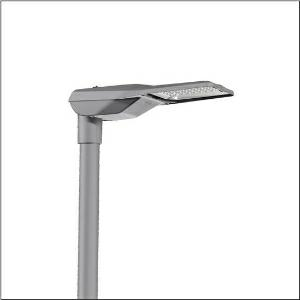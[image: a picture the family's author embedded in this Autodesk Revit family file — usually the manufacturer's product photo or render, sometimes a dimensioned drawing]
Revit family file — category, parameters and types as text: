
# Revit family: streetlight_sl_21_mini___p0_8a_5xe2u33s08gb_2c4a
name_source: partatom
category: Lighting Fixtures
units: mm (PartAtom-declared; Revit-internal decimal feet)

## family parameters
Cut with Voids When Loaded = No
Host = Face
Light Source = No
Part Type = Normal
Room Calculation Point = No
Round Connector Dimension = Use Diameter
Shared = No

## types (1)
- --- (1 x LED, 5990 lm, 40.4 W, 3000K)
    Apparent Load = 40 VA
    CIE Flux Codes = 33 69 96 100 100
    Color Rendering = 70
    Color Temperature = 3000K
    Default Elevation = 1800 mm
    Description = Streetlight SL 21 mini, mast luminaire, primary light control with lens, of PMMA, primary optical cover: cover, of toughened safety glass, transparent, light distribution: P0.8a, light emission: direct distribution, primary light characteristic: asymmetric, installation type: post-top, side-entry, LED, High Power LED, rated luminous flux: 5.990lm, luminous efficacy: 148lm/W, light colour: 730, colour temperature: 3000K, control gear: D4i, control: pre-setting: logarithmic dimming characteristic, flexible luminous flux parameterisation, time-dependent luminous flux control, constant luminous flux control, overheat protection, mains connection: 220..240V, AC, 50/60Hz, start of lifetime: 40W, end of service life: 41W, reduction: 19W, luminaire housing, of diecast aluminium, powder-coated, SITECO metallic grey (DB 702S), corrosivity category C5 high according to DIN EN ISO 12944, multi-level sealing system, sealing non-destructively replaceable, inclination adjustable: 0°, 5°, 10°, 15°, please order mast flange separately, length: 628mm, width: 235mm, height: 110mm, mast flange for spigot size: 42mm (side-entry): 5XC10008XM4, 60/48mm (side-entry/post-top): 5XC10108XM2, 76/60mm (side-entry/post-top): 5XC10108XM1, mounting height: 4..8m, Smart Interface above, protection rating (complete): IP66, insulation class (complete): insulation class II (safety insulation), certification: CE, ENEC, ENEC+, VDE, impact resistance: IK10, permissible operating ambient temperature for outdoor applications: -40..+50°C, standard-compliant lighting for roads and squares, packaging unit: 1 piece

Light Distribution: P0.8a
    Height = 110 mm
    Lamp = 1 x LED
    Lamp Light Flux = 5990 lm
    Lamp Power = 40.4 W
    Lamp count = 1
    Length = 625 mm
    Luminous efficacy = 148 lm/W
    Manufacturer = Siteco
    ModVariant = No
    Model = 5XE2U33S08GB
    Number of Poles = 1
    OnlyDefault = Yes
    Power Factor = 1
    Product Name = Streetlight SL 21 mini | P0.8a
    Product group = mast luminaire | pylon top
    ProductGroupID = 6100
    Protection Class = Protection class II
    Protection Degree = IP 66
    RLX_Detail_Level = 1
    RLX_Emergency_Light_Flux = 0 lm
    RLX_Emergency_Type = 0
    RLX_Emergency_Type_DB = No
    RlxData = <blob elided: 92921 chars, md5=464df9af>
    Socket = socket
    Standby Power = 0 W
    System Light Flux = 5990 lm
    System Power = 40 W
    Type Comments = factory setting: luminous flux: 100 % | dim-lin: 254 | 812 mA
    Type Image = l_1003515.jpg
    URL = http://relux.com
    VarID = @adj_079991
    Voltage = 0 V
    Weight = 0.00 kg
    Width = 234 mm

## geometry (parser evidence)
native form markers: Blend x4, Sweep x13
no freeform markers — native parametric forms only
